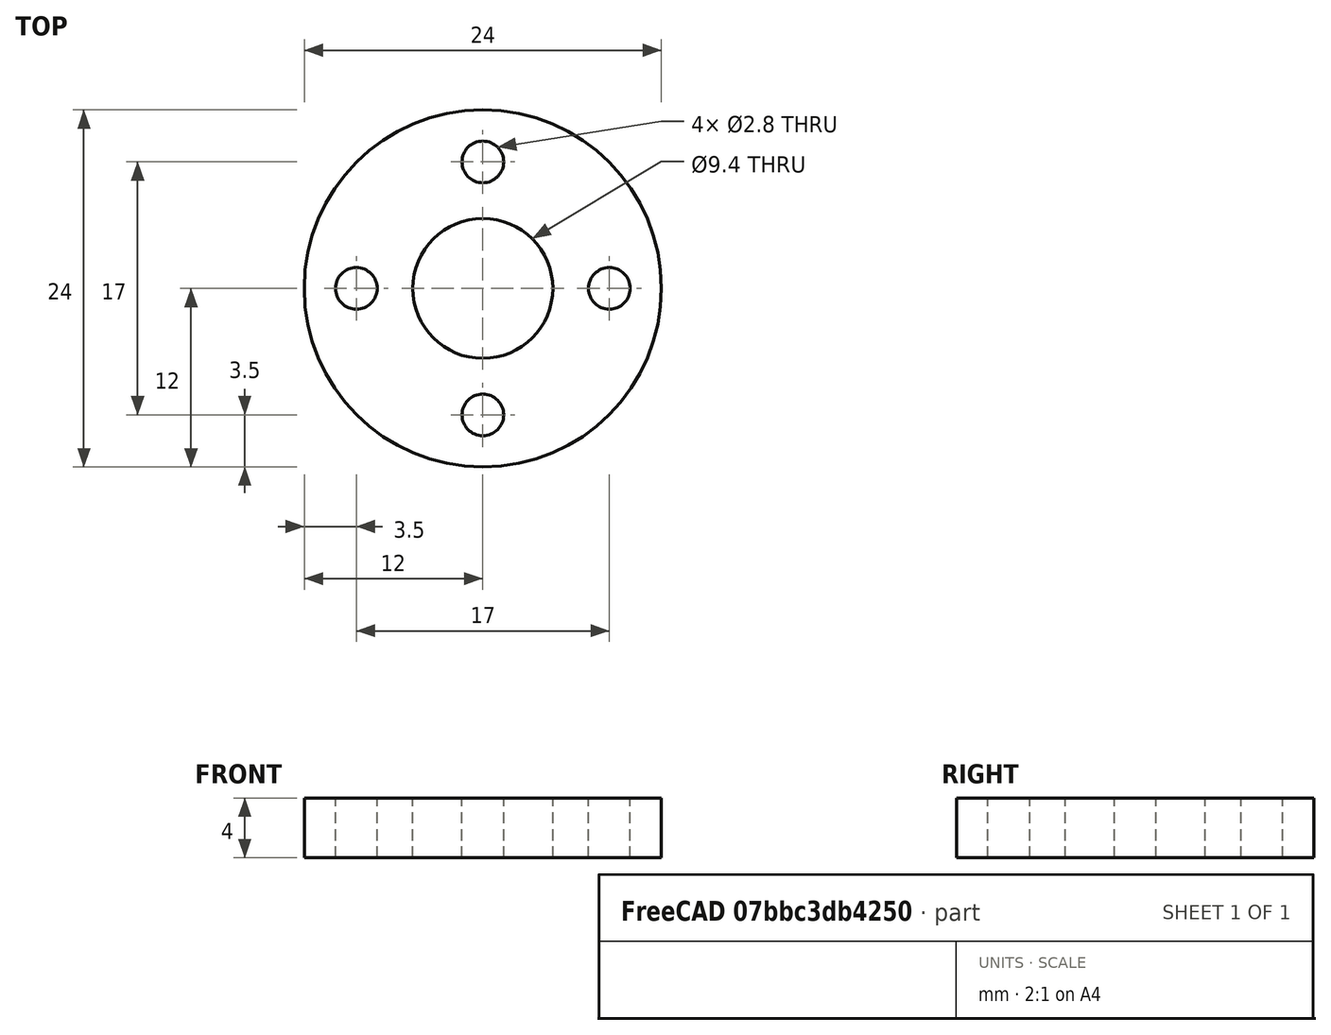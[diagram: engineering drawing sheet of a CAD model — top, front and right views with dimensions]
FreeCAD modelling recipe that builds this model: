
FCSTD DOCUMENT  (FreeCAD 0.16R6703 (Git))
Label: bearing-holder
License: All rights reserved
LicenseURL: http://en.wikipedia.org/wiki/All_rights_reserved
objects: Part::Cylinder×6, Part::Cut×5
note: 11 computed .brp shape members not serialized (recipe doc carries the construction recipe); baked Part::Feature solids carry a one-line shape summary decoded from their .brp

FEATURE [Part::Cylinder] Cylinder
  Angle = 360
  Height = 4
  Radius = 12
FEATURE [Part::Cylinder] Cylinder002
  Angle = 360
  Height = 10
  Placement = pos=(-8.5,0,-1) rot=(0,0,1;0rad)
  Radius = 1.4
FEATURE [Part::Cylinder] Cylinder003
  Angle = 360
  Height = 10
  Placement = pos=(8.5,0,-1) rot=(0,0,1;0rad)
  Radius = 1.4
FEATURE [Part::Cylinder] Cylinder004
  Angle = 360
  Height = 10
  Placement = pos=(0,8.5,-1) rot=(0,0,1;0rad)
  Radius = 1.4
FEATURE [Part::Cylinder] Cylinder005
  Angle = 360
  Height = 10
  Placement = pos=(0,-8.5,-1) rot=(0,0,1;0rad)
  Radius = 1.4
FEATURE [Part::Cut] Cut
  Base = -> Cylinder
  Tool = -> Cylinder002
FEATURE [Part::Cut] Cut001
  Base = -> Cut
  Tool = -> Cylinder005
FEATURE [Part::Cut] Cut002
  Base = -> Cut001
  Tool = -> Cylinder004
FEATURE [Part::Cut] Cut003
  Base = -> Cut002
  Tool = -> Cylinder003
FEATURE [Part::Cylinder] Cylinder006
  Angle = 360
  Height = 6
  Placement = pos=(0,0,-1) rot=(0,0,1;0rad)
  Radius = 4.7
FEATURE [Part::Cut] Cut004  label="mr93zz-bearing-holder"
  Base = -> Cut003
  Tool = -> Cylinder006
